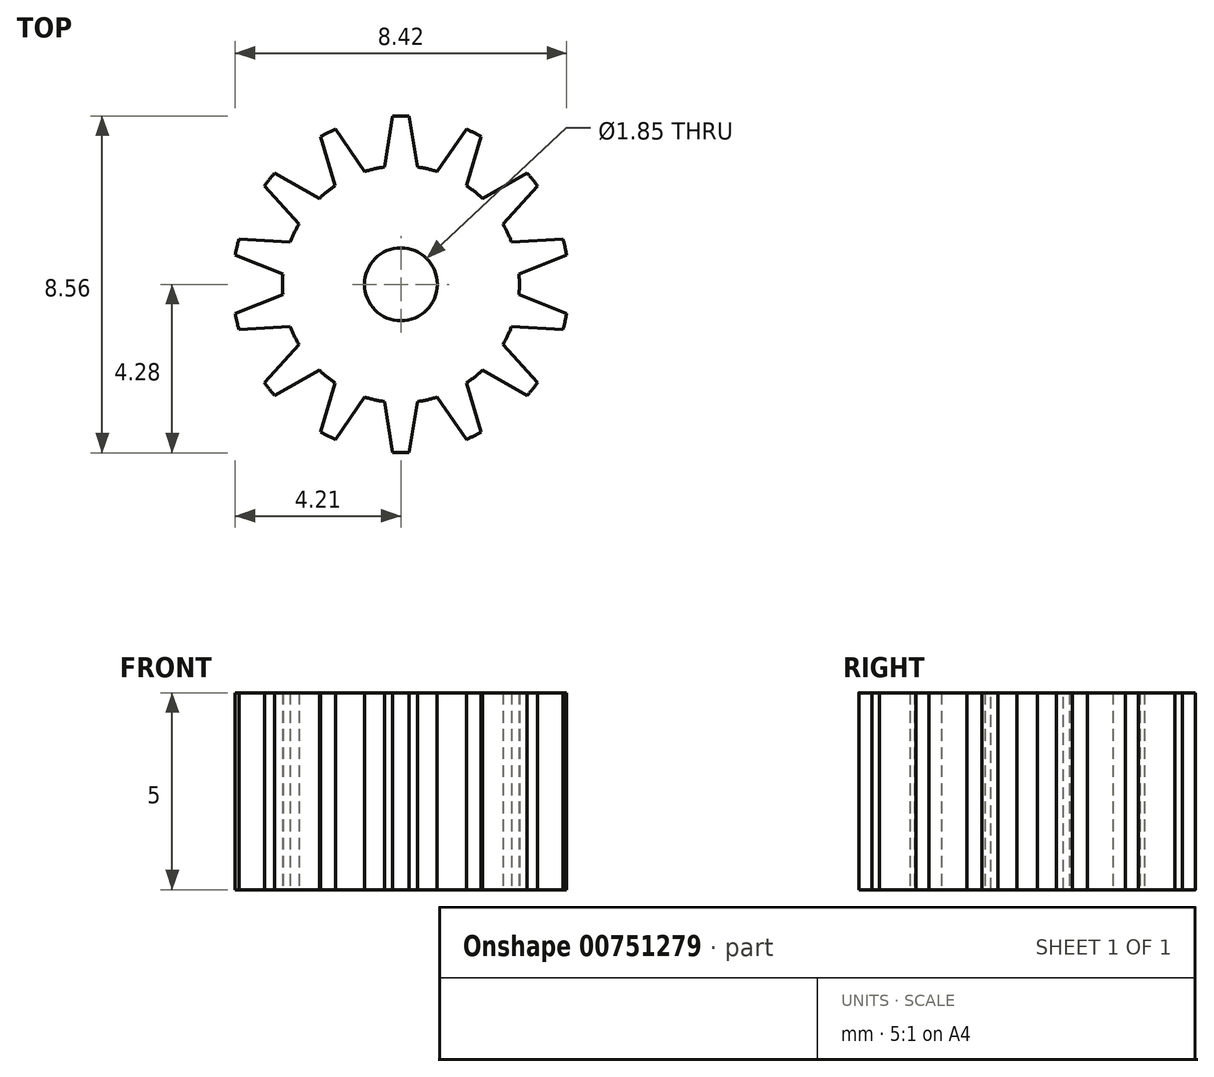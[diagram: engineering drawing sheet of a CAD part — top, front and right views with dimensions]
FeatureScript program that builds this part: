
annotation { "Feature Type Name" : "Feature", "Feature Type Description" : "" }
export const myFeature = defineFeature(function(context is Context, id is Id, definition is map)
    precondition{}
    {
        {
            assignVariable(context, id + "F0", {"name" : "teeth", "anyValue" : 14});
        }
        {
            var Q0;
            Q0=qCreatedBy(makeId("Top.planeOp"),FACE);
            var sketch = newSketch(context, id + "F1", { "sketchPlane" : qUnion([Q0])});
            skCircle(sketch, "E0", {"center": v(0, 0) * mm, "radius": 3 * mm});
            skCircle(sketch, "E1", {"center": v(0, 0) * mm, "radius": 4.28 * mm});
            skLineSegment(sketch, "E2", {"start": v(0.42, 2.98) * mm, "end": v(0.2, 4.27) * mm});
            skLineSegment(sketch, "E3", {"start": v(-0.42, 2.98) * mm, "end": v(-0.2, 4.27) * mm});
            skLineSegment(sketch, "E4", {"start": v(0, 0) * mm, "end": v(0, 64.06) * mm, "construction": true});
            skArc(sketch, "E5", {"start": v(-0.42, 2.98) * mm, "mid": v(-0.2, 3) * mm, "end": v(0, 3) * mm});
            skArc(sketch, "E6", {"start": v(0.42, 2.98) * mm, "mid": v(0.2, 3) * mm, "end": v(0, 3) * mm});
            skCircle(sketch, "E7", {"center": v(0, 0) * mm, "radius": 3.63 * mm, "construction": true});
            skPoint(sketch, "E8", {"position": v(-0.31, 3.62) * mm});
            skArc(sketch, "E9", {"start": v(0.2, 4.27) * mm, "mid": v(0.1, 4.27) * mm, "end": v(0, 4.28) * mm});
            skArc(sketch, "E10", {"start": v(-0.2, 4.27) * mm, "mid": v(-0.1, 4.27) * mm, "end": v(0, 4.28) * mm});
            skPoint(sketch, "E11", {"position": v(0.31, 3.62) * mm});
            skSolve(sketch);
        }
        {
            var Q0;
            Q0=qCreatedBy(makeId("Right.planeOp"),FACE);
            var sketch = newSketch(context, id + "F2", { "sketchPlane" : qUnion([Q0])});
            skLineSegment(sketch, "E12", {"start": v(0, 16.96) * mm, "end": v(0, -9.96) * mm, "construction": true});
            skSolve(sketch);
        }
        {
            var Q0;
            {var subQ0=sQuery(id+"F1.wireOp",EDGE,"E0");var subQ1=makeQuery(id+"F1.imprint","INTERSECT",VERTEX,{"derivedFrom":[subQ0,sQuery(id+"F1.wireOp",EDGE,"E2")]});Q0=makeQuery(id+"F1.imprint","IMPRINT",FACE,{"disambiguationData":[TD([[makeQuery(id+"F1.imprint","IMPRINT",EDGE,{"disambiguationData":[TD([[subQ1,-1.0]])],"derivedFrom":subQ0}),1.0]])]});}
            extrude(context, id + "F3", {"entities" : qUnion([Q0]), "depth" : 5 * mm, "offsetDistance" : 25 * mm});
        }
        {
            var Q0;
            {var subQ0=sQuery(id+"F1.wireOp",EDGE,"E2");Q0=makeQuery(id+"F1.imprint","IMPRINT",FACE,{"disambiguationData":[TD([[makeQuery(id+"F1.imprint","IMPRINT",EDGE,{"derivedFrom":subQ0}),1.0]])]});}
            extrude(context, id + "F4", {"entities" : qUnion([Q0]), "operationType" : NewBodyOperationType.ADD, "depth" : 5 * mm, "offsetDistance" : 25 * mm});
        }
        {
            var Q0;
            Q0=makeQuery(id+"F3.opExtrude","SWEPT_BODY",BODY,{"disambiguationData":[OSD([sQuery(id+"F1.wireOp",EDGE,"E0")])]});
            var Q1;
            Q1=sQuery(id+"F2.wireOp",EDGE,"E12");
            circularPattern(context, id + "F5", {"operationType" : NewBodyOperationType.ADD, "entities" : qUnion([Q0]), "axis" : qUnion([Q1]), "angle" : 360 * degree, "instanceCount" : getVariable(context, 'teeth'), "equalSpace" : true});
        }
        {
            var Q0;
            {var subQ0=sQuery(id+"F1.wireOp",EDGE,"E0");var subQ1=makeQuery(id+"F4.boolean.opBoolean","MERGE",FACE,{"derivedFrom":[makeQuery(id+"F3.opExtrude","CAP_FACE",FACE,{"disambiguationData":[OSD([subQ0])],"isStart":false}),makeQuery(id+"F4.opExtrude","CAP_FACE",FACE,{"disambiguationData":[OSD([subQ0,sQuery(id+"F1.wireOp",EDGE,"E1"),sQuery(id+"F1.wireOp",EDGE,"E2"),sQuery(id+"F1.wireOp",EDGE,"E3")])],"isStart":false})]});Q0=makeQuery(id+"F5.boolean.opBoolean","MERGE",FACE,{"derivedFrom":[subQ1,makeQuery(id+"F5.opPattern","COPY",FACE,{"derivedFrom":subQ1,"instanceName":"1"}),makeQuery(id+"F5.opPattern","COPY",FACE,{"derivedFrom":subQ1,"instanceName":"2"}),makeQuery(id+"F5.opPattern","COPY",FACE,{"derivedFrom":subQ1,"instanceName":"3"}),makeQuery(id+"F5.opPattern","COPY",FACE,{"derivedFrom":subQ1,"instanceName":"4"}),makeQuery(id+"F5.opPattern","COPY",FACE,{"derivedFrom":subQ1,"instanceName":"5"}),makeQuery(id+"F5.opPattern","COPY",FACE,{"derivedFrom":subQ1,"instanceName":"6"}),makeQuery(id+"F5.opPattern","COPY",FACE,{"derivedFrom":subQ1,"instanceName":"7"}),makeQuery(id+"F5.opPattern","COPY",FACE,{"derivedFrom":subQ1,"instanceName":"8"}),makeQuery(id+"F5.opPattern","COPY",FACE,{"derivedFrom":subQ1,"instanceName":"9"}),makeQuery(id+"F5.opPattern","COPY",FACE,{"derivedFrom":subQ1,"instanceName":"10"}),makeQuery(id+"F5.opPattern","COPY",FACE,{"derivedFrom":subQ1,"instanceName":"11"}),makeQuery(id+"F5.opPattern","COPY",FACE,{"derivedFrom":subQ1,"instanceName":"12"}),makeQuery(id+"F5.opPattern","COPY",FACE,{"derivedFrom":subQ1,"instanceName":"13"}),makeQuery(id+"F5.opPattern","COPY",FACE,{"derivedFrom":subQ1,"instanceName":"14"}),makeQuery(id+"F5.opPattern","COPY",FACE,{"derivedFrom":subQ1,"instanceName":"15"}),makeQuery(id+"F5.opPattern","COPY",FACE,{"derivedFrom":subQ1,"instanceName":"16"}),makeQuery(id+"F5.opPattern","COPY",FACE,{"derivedFrom":subQ1,"instanceName":"17"}),makeQuery(id+"F5.opPattern","COPY",FACE,{"derivedFrom":subQ1,"instanceName":"18"}),makeQuery(id+"F5.opPattern","COPY",FACE,{"derivedFrom":subQ1,"instanceName":"19"}),makeQuery(id+"F5.opPattern","COPY",FACE,{"derivedFrom":subQ1,"instanceName":"20"}),makeQuery(id+"F5.opPattern","COPY",FACE,{"derivedFrom":subQ1,"instanceName":"21"}),makeQuery(id+"F5.opPattern","COPY",FACE,{"derivedFrom":subQ1,"instanceName":"22"}),makeQuery(id+"F5.opPattern","COPY",FACE,{"derivedFrom":subQ1,"instanceName":"23"}),makeQuery(id+"F5.opPattern","COPY",FACE,{"derivedFrom":subQ1,"instanceName":"24"})]});}
            var sketch = newSketch(context, id + "F6", { "sketchPlane" : qUnion([Q0])});
            skCircle(sketch, "E13", {"center": v(0, 0) * mm, "radius": 0.93 * mm});
            skSolve(sketch);
        }
        {
            var Q0;
            Q0=makeQuery(id+"F6.imprint","IMPRINT",FACE,{"disambiguationData":[TD([[makeQuery(id+"F6.imprint","IMPRINT",EDGE,{"derivedFrom":sQuery(id+"F6.wireOp",EDGE,"E13")}),1.0]])]});
            extrude(context, id + "F7", {"entities" : qUnion([Q0]), "operationType" : NewBodyOperationType.REMOVE, "endBound" : BoundingType.THROUGH_ALL, "oppositeDirection" : true, "depth" : 25 * mm, "offsetDistance" : 25 * mm});
        }
    });
